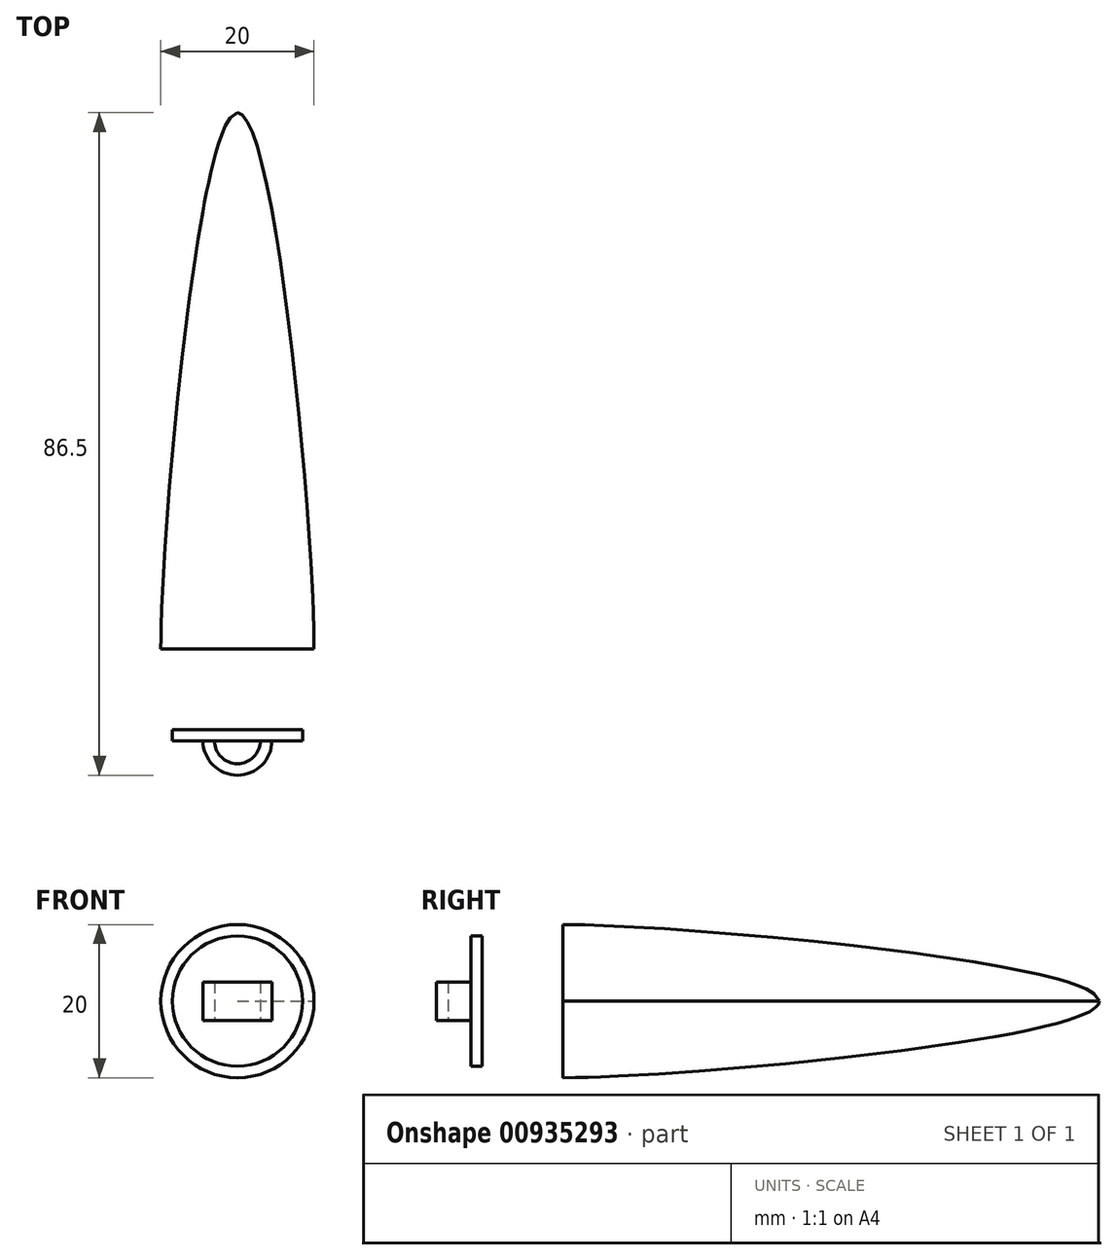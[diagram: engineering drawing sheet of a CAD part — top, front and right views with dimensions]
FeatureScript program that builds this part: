
annotation { "Feature Type Name" : "Feature", "Feature Type Description" : "" }
export const myFeature = defineFeature(function(context is Context, id is Id, definition is map)
    precondition{}
    {
        {
            var Q0;
            Q0=qCreatedBy(makeId("Top.planeOp"),FACE);
            var sketch = newSketch(context, id + "F0", { "sketchPlane" : qUnion([Q0])});
            skLineSegment(sketch, "E0", {"start": v(0, 0) * mm, "end": v(0, 70) * mm});
            skLineSegment(sketch, "E1", {"start": v(10, 0) * mm, "end": v(0, 0) * mm});
            skFitSpline(sketch, "E2", {"points": [v(0, 70) * mm, v(10, 0) * mm], "startDerivative": vector(15, 0) * mm, "endDerivative": vector(0, -48) * mm});
            skFitSpline(sketch, "E3.0", {"points": [v(-0.5, 68.7) * mm, v(-0.49, 68.7) * mm, v(-0.46, 68.67) * mm, v(-0.42, 68.64) * mm, v(-0.4, 68.62) * mm, v(-0.38, 68.61) * mm, v(-0.37, 68.6) * mm, v(-0.37, 68.6) * mm, v(-0.36, 68.6) * mm, v(-0.36, 68.6) * mm, v(-0.36, 68.6) * mm, v(-0.36, 68.6) * mm, v(-0.36, 68.6) * mm, v(-0.36, 68.6) * mm, v(-0.35, 68.58) * mm, v(-0.32, 68.56) * mm, v(-0.28, 68.52) * mm, v(-0.22, 68.44) * mm, v(-0.13, 68.3) * mm, v(0.01, 68.08) * mm, v(0.2, 67.72) * mm, v(0.46, 67.15) * mm, v(0.8, 66.25) * mm, v(1.22, 64.93) * mm, v(1.65, 63.38) * mm, v(2.07, 61.62) * mm, v(2.63, 59.04) * mm, v(3.32, 55.39) * mm, v(4.1, 50.48) * mm, v(4.85, 45.16) * mm, v(5.55, 39.57) * mm, v(6.19, 33.82) * mm, v(6.96, 26.12) * mm, v(7.75, 16.74) * mm, v(8.35, 6.88) * mm, v(8.5, 1.9) * mm, v(8.5, 0) * mm]});
            skLineSegment(sketch, "E4.bottom", {"start": v(8.5, 0) * mm, "end": v(7.87, 0) * mm});
            skLineSegment(sketch, "E5.bottom", {"start": v(7.87, 0) * mm, "end": v(9.12, 0) * mm});
            skLineSegment(sketch, "E5.top", {"start": v(7.88, -12) * mm, "end": v(9.12, -12) * mm});
            skLineSegment(sketch, "E5.left", {"start": v(7.88, 0) * mm, "end": v(7.88, -12) * mm});
            skLineSegment(sketch, "E5.right", {"start": v(9.12, 0) * mm, "end": v(9.12, -12) * mm});
            skLineSegment(sketch, "E6.bottom", {"start": v(7.87, 0) * mm, "end": v(9.15, 0) * mm});
            skLineSegment(sketch, "E6.left", {"start": v(7.87, 0) * mm, "end": v(7.87, 1.5) * mm});
            skLineSegment(sketch, "E7.right", {"start": v(9.12, 0) * mm, "end": v(9.12, 1.5) * mm});
            skLineSegment(sketch, "E8", {"start": v(9.12, 1.5) * mm, "end": v(7.87, 1.5) * mm});
            skLineSegment(sketch, "E9.bottom", {"start": v(8.5, -12) * mm, "end": v(0, -12) * mm});
            skLineSegment(sketch, "E9.top", {"start": v(8.5, -10.56) * mm, "end": v(0, -10.56) * mm});
            skLineSegment(sketch, "E9.left", {"start": v(8.5, -12) * mm, "end": v(8.5, -10.56) * mm});
            skLineSegment(sketch, "E9.right", {"start": v(0, -12) * mm, "end": v(0, -10.56) * mm});
            skSolve(sketch);
        }
        {
            var Q0;
            {var subQ6=sQuery(id+"F0.wireOp",EDGE,"E2");Q0=makeQuery(id+"F0.imprint","IMPRINT",FACE,{"disambiguationData":[TD([[makeQuery(id+"F0.imprint","IMPRINT",EDGE,{"derivedFrom":subQ6}),-1.0]])]});}
            var Q1;
            Q1=makeQuery(id+"F0.imprint","IMPRINT",FACE,{"disambiguationData":[TD([[makeQuery(id+"F0.imprint","IMPRINT",EDGE,{"derivedFrom":sQuery(id+"F0.wireOp",EDGE,"E5.top")}),1.0]])]});
            var Q2;
            {var subQ5=sQuery(id+"F0.wireOp",EDGE,"E6.left");Q2=makeQuery(id+"F0.imprint","IMPRINT",FACE,{"disambiguationData":[TD([[makeQuery(id+"F0.imprint","IMPRINT",EDGE,{"derivedFrom":subQ5}),-1.0]])]});}
            var Q3;
            {var subQ5=sQuery(id+"F0.wireOp",EDGE,"E7.right");Q3=makeQuery(id+"F0.imprint","IMPRINT",FACE,{"disambiguationData":[TD([[makeQuery(id+"F0.imprint","IMPRINT",EDGE,{"derivedFrom":subQ5}),1.0]])]});}
            var Q4;
            {var subQ5=sQuery(id+"F0.wireOp",EDGE,"E9.right");Q4=makeQuery(id+"F0.imprint","IMPRINT",FACE,{"disambiguationData":[TD([[makeQuery(id+"F0.imprint","IMPRINT",EDGE,{"derivedFrom":subQ5}),-1.0]])]});}
            var Q5;
            {var subQ5=sQuery(id+"F0.wireOp",EDGE,"E9.left");Q5=makeQuery(id+"F0.imprint","IMPRINT",FACE,{"disambiguationData":[TD([[makeQuery(id+"F0.imprint","IMPRINT",EDGE,{"derivedFrom":subQ5}),1.0]])]});}
            var Q6;
            Q6=sQuery(id+"F0.wireOp",EDGE,"E2");
            var Q7;
            Q7=sQuery(id+"F0.wireOp",EDGE,"E3.0");
            var Q8;
            Q8=sQuery(id+"F0.wireOp",EDGE,"E8");
            var Q9;
            Q9=sQuery(id+"F0.wireOp",EDGE,"E7.right");
            var Q10;
            Q10=sQuery(id+"F0.wireOp",EDGE,"E6.left");
            var Q11;
            Q11=sQuery(id+"F0.wireOp",EDGE,"E5.left");
            var Q12;
            Q12=sQuery(id+"F0.wireOp",EDGE,"E5.right");
            var Q13;
            Q13=sQuery(id+"F0.wireOp",EDGE,"E0");
            revolve(context, id + "F1", {"surfaceOperationType" : NewSurfaceOperationType.NEW, "entities" : qUnion([Q0, Q1, Q2, Q3, Q4, Q5]), "surfaceEntities" : qUnion([Q6, Q7, Q8, Q9, Q10, Q11, Q12]), "axis" : qUnion([Q13]), "revolveType" : RevolveType.FULL});
        }
        {
            var Q0;
            Q0=qCreatedBy(makeId("Top.planeOp"),FACE);
            var sketch = newSketch(context, id + "F2", { "sketchPlane" : qUnion([Q0])});
            skLineSegment(sketch, "E10.0", {"start": v(9.12, -12) * mm, "end": v(-9.12, -12) * mm});
            skArc(sketch, "E11", {"start": v(-3, -12) * mm, "mid": v(0, -15) * mm, "end": v(3, -12) * mm});
            skArc(sketch, "E12.0", {"start": v(-4.5, -12) * mm, "mid": v(0, -16.5) * mm, "end": v(4.5, -12) * mm});
            skSolve(sketch);
        }
        {
            var Q0;
            {var subQ0=sQuery(id+"F2.wireOp",EDGE,"E11");Q0=makeQuery(id+"F2.imprint","IMPRINT",FACE,{"disambiguationData":[TD([[makeQuery(id+"F2.imprint","IMPRINT",EDGE,{"derivedFrom":subQ0}),-1.0]])]});}
            extrude(context, id + "F3", {"entities" : qUnion([Q0]), "operationType" : NewBodyOperationType.ADD, "depth" : 2.5 * mm, "offsetDistance" : 25 * mm, "hasSecondDirection" : true, "secondDirectionOppositeDirection" : true, "secondDirectionDepth" : 2.5 * mm});
        }
    });
